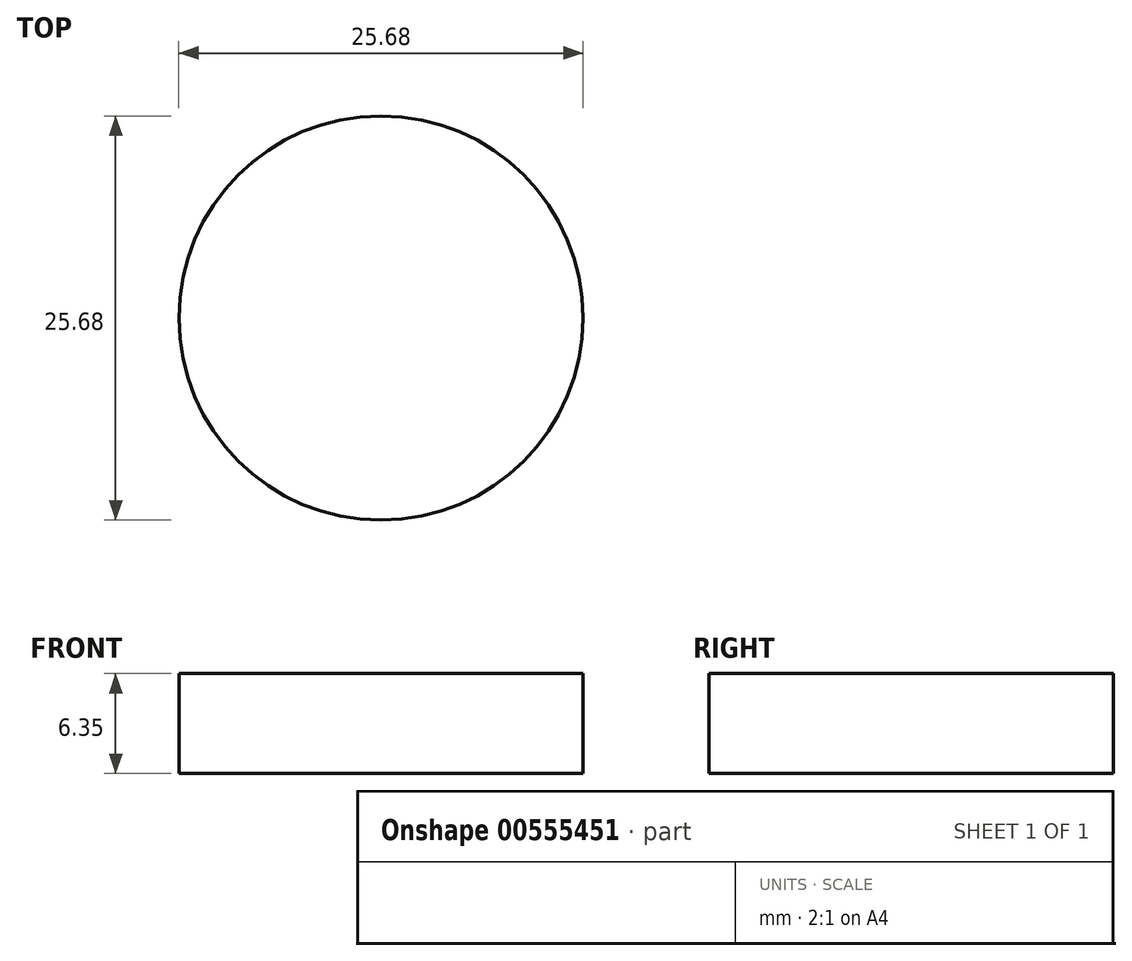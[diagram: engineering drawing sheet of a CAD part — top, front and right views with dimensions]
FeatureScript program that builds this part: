
annotation { "Feature Type Name" : "Feature", "Feature Type Description" : "" }
export const myFeature = defineFeature(function(context is Context, id is Id, definition is map)
    precondition{}
    {
        {
            var Q0;
            Q0=qCreatedBy(makeId("Top.planeOp"),FACE);
            var sketch = newSketch(context, id + "F0", { "sketchPlane" : qUnion([Q0])});
            skCircle(sketch, "E0", {"center": v(0, 0) * mm, "radius": 12.84 * mm});
            skSolve(sketch);
        }
        {
            var Q0;
            Q0 = qSketchRegion(id + "F0", true);
            extrude(context, id + "F1", {"entities" : qUnion([Q0]), "depth" : 6.35 * mm, "offsetDistance" : 25.4 * mm});
        }
    });
